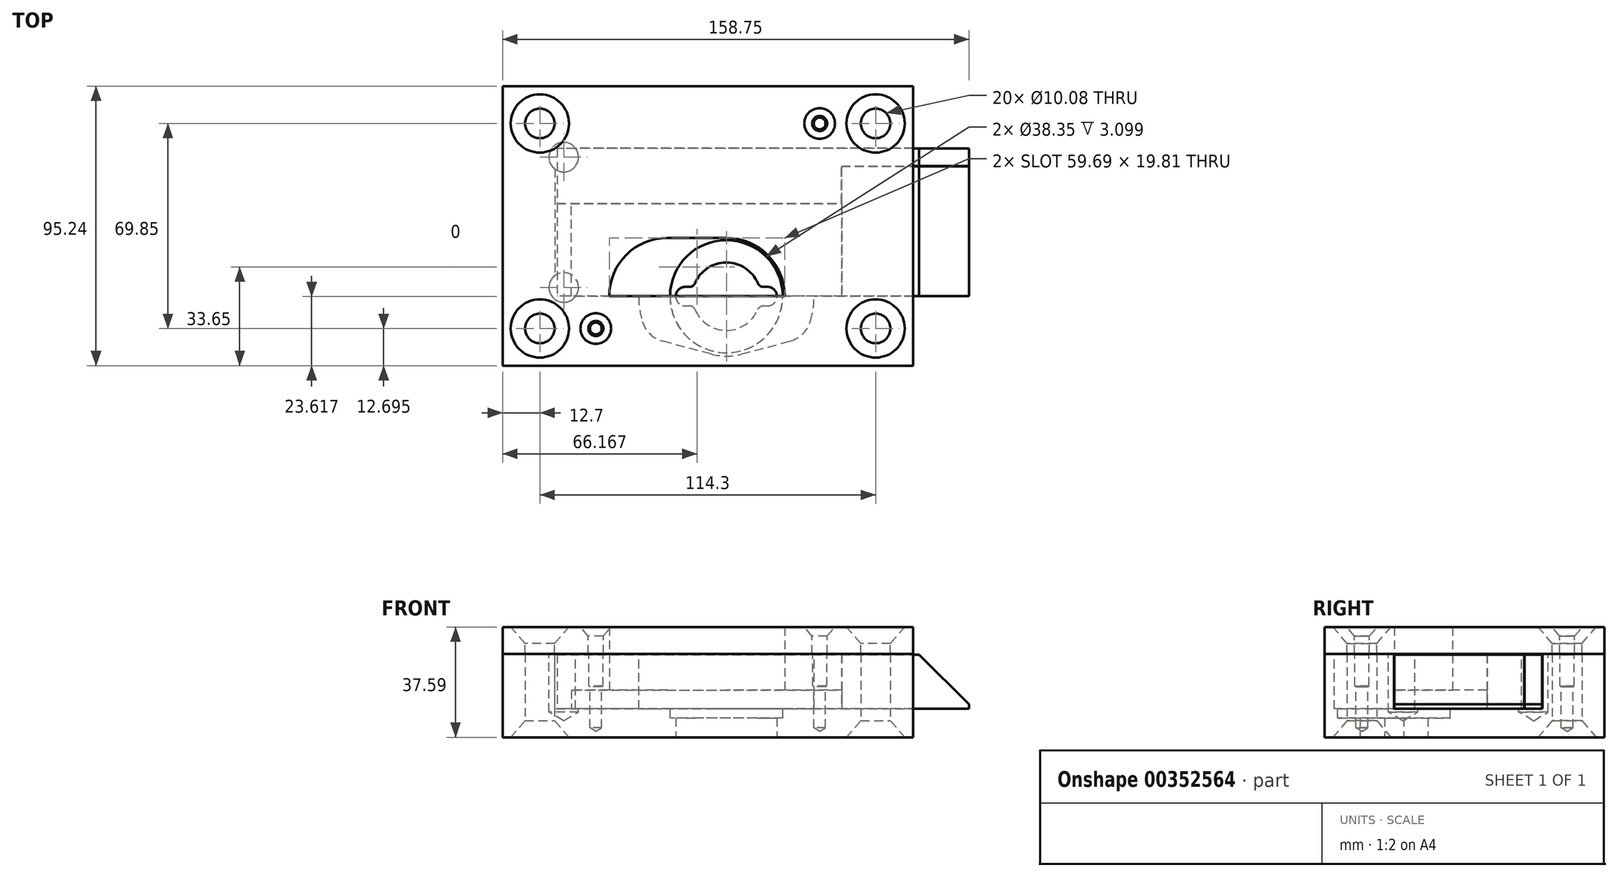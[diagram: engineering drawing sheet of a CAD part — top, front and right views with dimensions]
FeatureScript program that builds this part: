
annotation { "Feature Type Name" : "Feature", "Feature Type Description" : "" }
export const myFeature = defineFeature(function(context is Context, id is Id, definition is map)
    precondition{}
    {
        {
            var Q0;
            Q0=qCreatedBy(makeId("Top.planeOp"),FACE);
            cPlane(context, id + "F0", {"entities" : qUnion([Q0]), "cplaneType" : CPlaneType.OFFSET, "offset" : 6.6 * mm, "oppositeDirection" : true, "width" : 152.4 * mm, "height" : 152.4 * mm});
        }
        {
            var Q0;
            Q0=qCreatedBy(id+"F0.planeOp",FACE);
            var sketch = newSketch(context, id + "F1", { "sketchPlane" : qUnion([Q0])});
            skLineSegment(sketch, "E0.bottom", {"start": v(-69.85, 47.63) * mm, "end": v(69.85, 47.62) * mm});
            skLineSegment(sketch, "E0.top", {"start": v(-69.85, -47.62) * mm, "end": v(69.85, -47.63) * mm});
            skLineSegment(sketch, "E0.left", {"start": v(-69.85, 47.62) * mm, "end": v(-69.85, -47.63) * mm});
            skLineSegment(sketch, "E0.right", {"start": v(69.85, 47.63) * mm, "end": v(69.85, -47.62) * mm});
            skLineSegment(sketch, "E1", {"start": v(0, 47.63) * mm, "end": v(0, -47.63) * mm, "construction": true});
            skLineSegment(sketch, "E2", {"start": v(-69.85, 0) * mm, "end": v(69.85, 0) * mm, "construction": true});
            skPoint(sketch, "E3", {"position": v(-57.15, 34.93) * mm});
            skPoint(sketch, "E4", {"position": v(57.15, 34.93) * mm});
            skPoint(sketch, "E5", {"position": v(57.15, -34.93) * mm});
            skPoint(sketch, "E6", {"position": v(-57.15, -34.93) * mm});
            skArc(sketch, "E7", {"start": v(-4.32, -28.5) * mm, "mid": v(6.35, -35.59) * mm, "end": v(17.02, -28.5) * mm});
            skArc(sketch, "E8.0.startCap", {"start": v(-7.62, -27.25) * mm, "mid": v(-10.87, -24) * mm, "end": v(-7.62, -20.75) * mm});
            skArc(sketch, "E8.0.endCap", {"start": v(20.32, -20.75) * mm, "mid": v(23.57, -24) * mm, "end": v(20.32, -27.25) * mm});
            skLineSegment(sketch, "E8.0.left", {"start": v(-7.62, -20.75) * mm, "end": v(-6.2, -20.75) * mm});
            skLineSegment(sketch, "E8.0.right", {"start": v(-7.62, -27.25) * mm, "end": v(-6.2, -27.25) * mm});
            skLineSegment(sketch, "E9.trimOffspring", {"start": v(18.9, -20.75) * mm, "end": v(20.32, -20.75) * mm});
            skLineSegment(sketch, "E10.trimOffspring", {"start": v(18.9, -27.25) * mm, "end": v(20.32, -27.25) * mm});
            skArc(sketch, "E11.trimOffspring", {"start": v(17.02, -19.5) * mm, "mid": v(6.35, -12.42) * mm, "end": v(-4.32, -19.5) * mm});
            skPoint(sketch, "E12.visualSharp", {"position": v(-4.77, -27.25) * mm});
            skArc(sketch, "E12.filletArc", {"start": v(-4.32, -28.5) * mm, "mid": v(-5.07, -27.6) * mm, "end": v(-6.2, -27.25) * mm});
            skPoint(sketch, "E13.visualSharp", {"position": v(-4.77, -20.75) * mm});
            skArc(sketch, "E13.filletArc", {"start": v(-6.2, -20.75) * mm, "mid": v(-5.07, -20.41) * mm, "end": v(-4.32, -19.5) * mm});
            skPoint(sketch, "E14.visualSharp", {"position": v(17.47, -20.75) * mm});
            skArc(sketch, "E14.filletArc", {"start": v(17.02, -19.5) * mm, "mid": v(17.77, -20.41) * mm, "end": v(18.9, -20.75) * mm});
            skPoint(sketch, "E15.visualSharp", {"position": v(17.47, -27.25) * mm});
            skArc(sketch, "E15.filletArc", {"start": v(18.9, -27.25) * mm, "mid": v(17.77, -27.6) * mm, "end": v(17.02, -28.5) * mm});
            skLineSegment(sketch, "E16", {"start": v(-7.62, -24) * mm, "end": v(20.32, -24) * mm, "construction": true});
            skLineSegment(sketch, "E17", {"start": v(6.35, -9.05) * mm, "end": v(6.35, -38.96) * mm, "construction": true});
            skSolve(sketch);
        }
        {
            var Q0;
            Q0 = qSketchRegion(id + "F1", true);
            extrude(context, id + "F2", {"entities" : qUnion([Q0]), "depth" : 28.45 * mm});
        }
        {
            var Q0;
            Q0=sQuery(id+"F1.wireOp",VERTEX,"E6");
            var Q1;
            Q1=sQuery(id+"F1.wireOp",VERTEX,"E5");
            var Q2;
            Q2=sQuery(id+"F1.wireOp",VERTEX,"E4");
            var Q3;
            Q3=sQuery(id+"F1.wireOp",VERTEX,"E3");
            var Q4;
            Q4=makeQuery(id+"F2.opExtrude","SWEPT_BODY",BODY,{"disambiguationData":[OSD([sQuery(id+"F1.wireOp",EDGE,"E0.bottom"),sQuery(id+"F1.wireOp",EDGE,"E0.top"),sQuery(id+"F1.wireOp",EDGE,"E0.left"),sQuery(id+"F1.wireOp",EDGE,"E0.right"),sQuery(id+"F1.wireOp",EDGE,"E7"),sQuery(id+"F1.wireOp",EDGE,"E8.0.startCap"),sQuery(id+"F1.wireOp",EDGE,"E8.0.endCap"),sQuery(id+"F1.wireOp",EDGE,"E8.0.left"),sQuery(id+"F1.wireOp",EDGE,"E8.0.right"),sQuery(id+"F1.wireOp",EDGE,"E9.trimOffspring"),sQuery(id+"F1.wireOp",EDGE,"E10.trimOffspring"),sQuery(id+"F1.wireOp",EDGE,"E11.trimOffspring"),sQuery(id+"F1.wireOp",EDGE,"E12.filletArc"),sQuery(id+"F1.wireOp",EDGE,"E13.filletArc"),sQuery(id+"F1.wireOp",EDGE,"E14.filletArc"),sQuery(id+"F1.wireOp",EDGE,"E15.filletArc")])]});
            hole(context, id + "F3", {"style" : HoleStyle.C_SINK, "endStyle" : HoleEndStyle.THROUGH, "oppositeDirection" : true, "standardTappedOrClearance" : lookupTablePath({ "standard" : "ANSI", "fit" : "Normal (ASME)", "size" : "3/8", "type" : "Clearance" }), "standardBlindInLast" : lookupTablePath({ "fit" : "Free", "standard" : "ANSI", "size" : "3/8", "type" : "Clearance" }), "holeDiameter" : 10.08 * mm, "cSinkDiameter" : 19.84 * mm, "cSinkAngle" : 82 * degree, "tappedDepth" : 9.65 * mm, "tapClearance" : 16, "locations" : qUnion([Q0, Q1, Q2, Q3]), "scope" : qUnion([Q4])});
        }
        {
            var Q0;
            Q0=makeQuery(id+"F2.opExtrude","CAP_FACE",FACE,{"disambiguationData":[OSD([sQuery(id+"F1.wireOp",EDGE,"E0.bottom"),sQuery(id+"F1.wireOp",EDGE,"E0.top"),sQuery(id+"F1.wireOp",EDGE,"E0.left"),sQuery(id+"F1.wireOp",EDGE,"E0.right"),sQuery(id+"F1.wireOp",EDGE,"E7"),sQuery(id+"F1.wireOp",EDGE,"E8.0.startCap"),sQuery(id+"F1.wireOp",EDGE,"E8.0.endCap"),sQuery(id+"F1.wireOp",EDGE,"E8.0.left"),sQuery(id+"F1.wireOp",EDGE,"E8.0.right"),sQuery(id+"F1.wireOp",EDGE,"E9.trimOffspring"),sQuery(id+"F1.wireOp",EDGE,"E10.trimOffspring"),sQuery(id+"F1.wireOp",EDGE,"E11.trimOffspring"),sQuery(id+"F1.wireOp",EDGE,"E12.filletArc"),sQuery(id+"F1.wireOp",EDGE,"E13.filletArc"),sQuery(id+"F1.wireOp",EDGE,"E14.filletArc"),sQuery(id+"F1.wireOp",EDGE,"E15.filletArc")])],"isStart":false});
            var sketch = newSketch(context, id + "F4", { "sketchPlane" : qUnion([Q0])});
            skLineSegment(sketch, "E18.bottom", {"start": v(69.85, 26.5) * mm, "end": v(-52.07, 26.5) * mm});
            skLineSegment(sketch, "E18.top", {"start": v(69.85, -24) * mm, "end": v(36.2, -24) * mm});
            skLineSegment(sketch, "E18.left", {"start": v(69.85, 26.5) * mm, "end": v(69.85, -24) * mm});
            skLineSegment(sketch, "E18.right", {"start": v(-52.07, 26.5) * mm, "end": v(-52.07, -24) * mm});
            skPoint(sketch, "E19", {"position": v(6.35, -24) * mm});
            skArc(sketch, "E20", {"start": v(34.97, -32.47) * mm, "mid": v(35.89, -28.28) * mm, "end": v(36.2, -24) * mm});
            skCircle(sketch, "E21", {"center": v(6.35, -24) * mm, "radius": 19.18 * mm});
            skLineSegment(sketch, "E22", {"start": v(11.6, -43.63) * mm, "end": v(28.03, -39.23) * mm});
            skLineSegment(sketch, "E23", {"start": v(1.1, -43.63) * mm, "end": v(-15.33, -39.23) * mm});
            skLineSegment(sketch, "E24", {"start": v(6.35, 12.67) * mm, "end": v(6.35, -59.04) * mm, "construction": true});
            skPoint(sketch, "E24.startSnap0", {"position": v(6.35, -12.42) * mm});
            skPoint(sketch, "E25.visualSharp", {"position": v(32.72, -37.97) * mm});
            skArc(sketch, "E25.filletArc", {"start": v(28.03, -39.23) * mm, "mid": v(32.38, -36.76) * mm, "end": v(34.97, -32.47) * mm});
            skPoint(sketch, "E26.visualSharp", {"position": v(-20.02, -37.97) * mm});
            skArc(sketch, "E26.filletArc", {"start": v(-22.27, -32.47) * mm, "mid": v(-19.68, -36.76) * mm, "end": v(-15.33, -39.23) * mm});
            skArc(sketch, "E27.trimOffspring", {"start": v(-23.5, -24) * mm, "mid": v(-23.19, -28.28) * mm, "end": v(-22.27, -32.47) * mm});
            skLineSegment(sketch, "E28.trimOffspring", {"start": v(-23.5, -24) * mm, "end": v(-52.07, -24) * mm});
            skArc(sketch, "E29.trimOffspring", {"start": v(1.1, -43.63) * mm, "mid": v(6.35, -44.32) * mm, "end": v(11.6, -43.63) * mm});
            skPoint(sketch, "E30", {"position": v(-44.96, 26.5) * mm});
            skPoint(sketch, "E31", {"position": v(-52.07, 19.38) * mm});
            skPoint(sketch, "E32", {"position": v(-52.07, -16.9) * mm});
            skPoint(sketch, "E33", {"position": v(-44.96, -24) * mm});
            skCircle(sketch, "E34", {"center": v(-49.02, -20.95) * mm, "radius": 5.08 * mm, "construction": true});
            skPoint(sketch, "E34.third.point", {"position": v(-45.45, -17.33) * mm});
            skCircle(sketch, "E35", {"center": v(-49.02, 23.44) * mm, "radius": 5.08 * mm, "construction": true});
            skPoint(sketch, "E35.third.point", {"position": v(-45.12, 20.19) * mm});
            skPoint(sketch, "E36", {"position": v(38.1, 34.93) * mm});
            skPoint(sketch, "E37", {"position": v(-38.1, -34.93) * mm});
            skPoint(sketch, "E38", {"position": v(57.15, 34.93) * mm});
            skPoint(sketch, "E39", {"position": v(-57.15, -34.93) * mm});
            skSolve(sketch);
        }
        {
            var Q0;
            Q0=makeQuery(id+"F4.imprint","IMPRINT",FACE,{"disambiguationData":[TD([[makeQuery(id+"F4.imprint","IMPRINT",EDGE,{"derivedFrom":sQuery(id+"F4.wireOp",EDGE,"E21")}),1.0]])]});
            extrude(context, id + "F5", {"entities" : qUnion([Q0]), "operationType" : NewBodyOperationType.REMOVE, "oppositeDirection" : true, "depth" : 21.84 * mm});
        }
        {
            var Q0;
            Q0=makeQuery(id+"F4.imprint","IMPRINT",FACE,{"disambiguationData":[TD([[makeQuery(id+"F4.imprint","IMPRINT",EDGE,{"derivedFrom":sQuery(id+"F4.wireOp",EDGE,"E18.bottom")}),1.0]])]});
            extrude(context, id + "F6", {"entities" : qUnion([Q0]), "operationType" : NewBodyOperationType.REMOVE, "oppositeDirection" : true, "depth" : 18.75 * mm});
        }
        {
            var Q0;
            Q0=sQuery(id+"F4.wireOp",VERTEX,"E35.center");
            var Q1;
            Q1=sQuery(id+"F4.wireOp",VERTEX,"E34.center");
            var Q2;
            Q2=makeQuery(id+"F2.opExtrude","SWEPT_BODY",BODY,{"disambiguationData":[OSD([sQuery(id+"F1.wireOp",EDGE,"E0.bottom"),sQuery(id+"F1.wireOp",EDGE,"E0.top"),sQuery(id+"F1.wireOp",EDGE,"E0.left"),sQuery(id+"F1.wireOp",EDGE,"E0.right"),sQuery(id+"F1.wireOp",EDGE,"E7"),sQuery(id+"F1.wireOp",EDGE,"E8.0.startCap"),sQuery(id+"F1.wireOp",EDGE,"E8.0.endCap"),sQuery(id+"F1.wireOp",EDGE,"E8.0.left"),sQuery(id+"F1.wireOp",EDGE,"E8.0.right"),sQuery(id+"F1.wireOp",EDGE,"E9.trimOffspring"),sQuery(id+"F1.wireOp",EDGE,"E10.trimOffspring"),sQuery(id+"F1.wireOp",EDGE,"E11.trimOffspring"),sQuery(id+"F1.wireOp",EDGE,"E12.filletArc"),sQuery(id+"F1.wireOp",EDGE,"E13.filletArc"),sQuery(id+"F1.wireOp",EDGE,"E14.filletArc"),sQuery(id+"F1.wireOp",EDGE,"E15.filletArc")])]});
            hole(context, id + "F7", {"style" : HoleStyle.SIMPLE, "endStyle" : HoleEndStyle.BLIND, "standardTappedOrClearance" : lookupTablePath({ "standard" : "ANSI", "size" : "X (0.4)", "type" : "Drilled" }), "standardBlindInLast" : lookupTablePath({ "standard" : "ANSI", "size" : "X", "type" : "Drilled" }), "holeDiameter" : 10.08 * mm, "holeDepth" : 19.8 * mm, "tappedDepth" : 9.65 * mm, "tapClearance" : 16, "startFromSketch" : true, "locations" : qUnion([Q0, Q1]), "scope" : qUnion([Q2])});
        }
        {
            var Q0;
            Q0=sQuery(id+"F4.wireOp",VERTEX,"E36");
            var Q1;
            Q1=sQuery(id+"F4.wireOp",VERTEX,"E37");
            var Q2;
            Q2=makeQuery(id+"F2.opExtrude","SWEPT_BODY",BODY,{"disambiguationData":[OSD([sQuery(id+"F1.wireOp",EDGE,"E0.bottom"),sQuery(id+"F1.wireOp",EDGE,"E0.top"),sQuery(id+"F1.wireOp",EDGE,"E0.left"),sQuery(id+"F1.wireOp",EDGE,"E0.right"),sQuery(id+"F1.wireOp",EDGE,"E7"),sQuery(id+"F1.wireOp",EDGE,"E8.0.startCap"),sQuery(id+"F1.wireOp",EDGE,"E8.0.endCap"),sQuery(id+"F1.wireOp",EDGE,"E8.0.left"),sQuery(id+"F1.wireOp",EDGE,"E8.0.right"),sQuery(id+"F1.wireOp",EDGE,"E9.trimOffspring"),sQuery(id+"F1.wireOp",EDGE,"E10.trimOffspring"),sQuery(id+"F1.wireOp",EDGE,"E11.trimOffspring"),sQuery(id+"F1.wireOp",EDGE,"E12.filletArc"),sQuery(id+"F1.wireOp",EDGE,"E13.filletArc"),sQuery(id+"F1.wireOp",EDGE,"E14.filletArc"),sQuery(id+"F1.wireOp",EDGE,"E15.filletArc")])]});
            hole(context, id + "F8", {"style" : HoleStyle.SIMPLE, "endStyle" : HoleEndStyle.BLIND, "standardTappedOrClearance" : lookupTablePath({ "standard" : "ANSI", "engagement" : "75%", "pitch" : "32 tpi", "size" : "#10", "type" : "Tapped" }), "standardBlindInLast" : lookupTablePath({ "standard" : "ANSI", "engagement" : "75%", "pitch" : "32 tpi", "size" : "#10", "type" : "Tapped" }), "holeDiameter" : 4.04 * mm, "showTappedDepth" : true, "holeDepth" : 25.2 * mm, "tappedDepth" : 10.92 * mm, "tapClearance" : 18, "locations" : qUnion([Q0, Q1]), "scope" : qUnion([Q2]), "majorDiameter" : 4.83 * mm});
        }
        {
            var Q0;
            Q0=sQuery(id+"F4.wireOp",VERTEX,"E36");
            var Q1;
            Q1=sQuery(id+"F4.wireOp",VERTEX,"E37");
            var Q2;
            Q2=makeQuery(id+"F2.opExtrude","SWEPT_BODY",BODY,{"disambiguationData":[OSD([sQuery(id+"F1.wireOp",EDGE,"E0.bottom"),sQuery(id+"F1.wireOp",EDGE,"E0.top"),sQuery(id+"F1.wireOp",EDGE,"E0.left"),sQuery(id+"F1.wireOp",EDGE,"E0.right"),sQuery(id+"F1.wireOp",EDGE,"E7"),sQuery(id+"F1.wireOp",EDGE,"E8.0.startCap"),sQuery(id+"F1.wireOp",EDGE,"E8.0.endCap"),sQuery(id+"F1.wireOp",EDGE,"E8.0.left"),sQuery(id+"F1.wireOp",EDGE,"E8.0.right"),sQuery(id+"F1.wireOp",EDGE,"E9.trimOffspring"),sQuery(id+"F1.wireOp",EDGE,"E10.trimOffspring"),sQuery(id+"F1.wireOp",EDGE,"E11.trimOffspring"),sQuery(id+"F1.wireOp",EDGE,"E12.filletArc"),sQuery(id+"F1.wireOp",EDGE,"E13.filletArc"),sQuery(id+"F1.wireOp",EDGE,"E14.filletArc"),sQuery(id+"F1.wireOp",EDGE,"E15.filletArc")])]});
            hole(context, id + "F9", {"style" : HoleStyle.C_SINK, "endStyle" : HoleEndStyle.BLIND, "holeDiameter" : 4.83 * mm, "cSinkDiameter" : 5.33 * mm, "cSinkAngle" : 90 * degree, "holeDepth" : 10.92 * mm, "tappedDepth" : 10.93 * mm, "tapClearance" : 18, "locations" : qUnion([Q0, Q1]), "scope" : qUnion([Q2])});
        }
        {
            var Q0;
            {var subQ8=sQuery(id+"F4.wireOp",EDGE,"E18.bottom");Q0=makeQuery(id+"F4.imprint","IMPRINT",FACE,{"disambiguationData":[TD([[makeQuery(id+"F4.imprint","IMPRINT",EDGE,{"derivedFrom":subQ8}),-1.0]])]});}
            var sketch = newSketch(context, id + "F10", { "sketchPlane" : qUnion([Q0])});
            skLineSegment(sketch, "E40.0", {"start": v(-69.85, 47.63) * mm, "end": v(69.85, 47.62) * mm});
            skLineSegment(sketch, "E41.0", {"start": v(-69.85, 47.63) * mm, "end": v(-69.85, -47.63) * mm});
            skLineSegment(sketch, "E42.0", {"start": v(-69.85, -47.62) * mm, "end": v(69.85, -47.63) * mm});
            skLineSegment(sketch, "E43", {"start": v(69.85, 47.62) * mm, "end": v(69.85, -47.63) * mm});
            skSolve(sketch);
        }
        {
            var Q0;
            Q0 = qSketchRegion(id + "F10", true);
            extrude(context, id + "F11", {"entities" : qUnion([Q0]), "depth" : 9.14 * mm});
        }
        {
            var Q0;
            Q0=makeQuery(id+"F11.opExtrude","CAP_FACE",FACE,{"disambiguationData":[OSD([sQuery(id+"F10.wireOp",EDGE,"E40.0"),sQuery(id+"F10.wireOp",EDGE,"E41.0"),sQuery(id+"F10.wireOp",EDGE,"E42.0"),sQuery(id+"F10.wireOp",EDGE,"E43")])],"isStart":false});
            var sketch = newSketch(context, id + "F12", { "sketchPlane" : qUnion([Q0])});
            skPoint(sketch, "E44", {"position": v(-57.15, 34.93) * mm});
            skPoint(sketch, "E45", {"position": v(57.15, 34.93) * mm});
            skPoint(sketch, "E46", {"position": v(57.15, -34.93) * mm});
            skPoint(sketch, "E47", {"position": v(-57.15, -34.93) * mm});
            skPoint(sketch, "E48", {"position": v(38.1, 34.93) * mm});
            skPoint(sketch, "E49", {"position": v(-38.1, -34.93) * mm});
            skSolve(sketch);
        }
        {
            var Q0;
            Q0=sQuery(id+"F12.wireOp",VERTEX,"E44");
            var Q1;
            Q1=sQuery(id+"F12.wireOp",VERTEX,"E45");
            var Q2;
            Q2=sQuery(id+"F12.wireOp",VERTEX,"E46");
            var Q3;
            Q3=sQuery(id+"F12.wireOp",VERTEX,"E47");
            var Q4;
            Q4=makeQuery(id+"F11.opExtrude","SWEPT_BODY",BODY,{"disambiguationData":[OSD([sQuery(id+"F10.wireOp",EDGE,"E40.0"),sQuery(id+"F10.wireOp",EDGE,"E41.0"),sQuery(id+"F10.wireOp",EDGE,"E42.0"),sQuery(id+"F10.wireOp",EDGE,"E43")])]});
            hole(context, id + "F13", {"style" : HoleStyle.C_SINK, "endStyle" : HoleEndStyle.THROUGH, "standardTappedOrClearance" : lookupTablePath({ "standard" : "ANSI", "fit" : "Normal (ASME)", "size" : "3/8", "type" : "Clearance" }), "standardBlindInLast" : lookupTablePath({ "fit" : "Free", "standard" : "ANSI", "size" : "3/8", "type" : "Clearance" }), "holeDiameter" : 10.08 * mm, "cSinkDiameter" : 19.84 * mm, "cSinkAngle" : 82 * degree, "tappedDepth" : 9.65 * mm, "tapClearance" : 16, "locations" : qUnion([Q0, Q1, Q2, Q3]), "scope" : qUnion([Q4])});
        }
        {
            var Q0;
            Q0=sQuery(id+"F12.wireOp",VERTEX,"E48");
            var Q1;
            Q1=sQuery(id+"F12.wireOp",VERTEX,"E49");
            var Q2;
            Q2=makeQuery(id+"F11.opExtrude","SWEPT_BODY",BODY,{"disambiguationData":[OSD([sQuery(id+"F10.wireOp",EDGE,"E40.0"),sQuery(id+"F10.wireOp",EDGE,"E41.0"),sQuery(id+"F10.wireOp",EDGE,"E42.0"),sQuery(id+"F10.wireOp",EDGE,"E43")])]});
            hole(context, id + "F14", {"style" : HoleStyle.C_SINK, "endStyle" : HoleEndStyle.THROUGH, "standardTappedOrClearance" : lookupTablePath({ "standard" : "ANSI", "fit" : "Normal (ASME)", "size" : "#10", "type" : "Clearance" }), "standardBlindInLast" : lookupTablePath({ "fit" : "Free", "standard" : "ANSI", "size" : "#10", "type" : "Clearance" }), "holeDiameter" : 5.1 * mm, "cSinkDiameter" : 10.44 * mm, "cSinkAngle" : 82 * degree, "tappedDepth" : 10.93 * mm, "tapClearance" : 18, "locations" : qUnion([Q0, Q1]), "scope" : qUnion([Q2])});
        }
        {
            var Q0;
            Q0=makeQuery(id+"F6.boolean.opBoolean","COPY",FACE,{"derivedFrom":makeQuery(id+"F6.opExtrude","CAP_FACE",FACE,{"disambiguationData":[OSD([sQuery(id+"F4.wireOp",EDGE,"E18.bottom"),sQuery(id+"F4.wireOp",EDGE,"E18.top"),sQuery(id+"F4.wireOp",EDGE,"E18.left"),sQuery(id+"F4.wireOp",EDGE,"E18.right"),sQuery(id+"F4.wireOp",EDGE,"E20"),sQuery(id+"F4.wireOp",EDGE,"E21"),sQuery(id+"F4.wireOp",EDGE,"E22"),sQuery(id+"F4.wireOp",EDGE,"E23"),sQuery(id+"F4.wireOp",EDGE,"E25.filletArc"),sQuery(id+"F4.wireOp",EDGE,"E26.filletArc"),sQuery(id+"F4.wireOp",EDGE,"E27.trimOffspring"),sQuery(id+"F4.wireOp",EDGE,"E28.trimOffspring"),sQuery(id+"F4.wireOp",EDGE,"E29.trimOffspring")])],"isStart":false})});
            var sketch = newSketch(context, id + "F15", { "sketchPlane" : qUnion([Q0])});
            skLineSegment(sketch, "E50", {"start": v(-51.3, 7.7) * mm, "end": v(45.47, 7.7) * mm});
            skLineSegment(sketch, "E51", {"start": v(45.47, 7.7) * mm, "end": v(45.47, 20.4) * mm});
            skLineSegment(sketch, "E52", {"start": v(45.47, 20.4) * mm, "end": v(88.9, 20.4) * mm});
            skLineSegment(sketch, "E53", {"start": v(88.9, 20.4) * mm, "end": v(88.9, 26.37) * mm});
            skLineSegment(sketch, "E54.0", {"start": v(88.9, 26.37) * mm, "end": v(-51.3, 26.37) * mm});
            skLineSegment(sketch, "E55.0", {"start": v(-51.3, 26.37) * mm, "end": v(-51.3, 7.7) * mm});
            skSolve(sketch);
        }
        {
            var Q0;
            Q0 = qSketchRegion(id + "F15", true);
            extrude(context, id + "F16", {"entities" : qUnion([Q0]), "depth" : 18.5 * mm});
        }
        {
            var Q0;
            Q0=makeQuery(id+"F6.boolean.opBoolean","COPY",FACE,{"derivedFrom":makeQuery(id+"F6.opExtrude","CAP_FACE",FACE,{"disambiguationData":[OSD([sQuery(id+"F4.wireOp",EDGE,"E18.bottom"),sQuery(id+"F4.wireOp",EDGE,"E18.top"),sQuery(id+"F4.wireOp",EDGE,"E18.left"),sQuery(id+"F4.wireOp",EDGE,"E18.right"),sQuery(id+"F4.wireOp",EDGE,"E20"),sQuery(id+"F4.wireOp",EDGE,"E21"),sQuery(id+"F4.wireOp",EDGE,"E22"),sQuery(id+"F4.wireOp",EDGE,"E23"),sQuery(id+"F4.wireOp",EDGE,"E25.filletArc"),sQuery(id+"F4.wireOp",EDGE,"E26.filletArc"),sQuery(id+"F4.wireOp",EDGE,"E27.trimOffspring"),sQuery(id+"F4.wireOp",EDGE,"E28.trimOffspring"),sQuery(id+"F4.wireOp",EDGE,"E29.trimOffspring")])],"isStart":false})});
            var sketch = newSketch(context, id + "F17", { "sketchPlane" : qUnion([Q0])});
            skLineSegment(sketch, "E56.0", {"start": v(-51.3, 7.57) * mm, "end": v(45.6, 7.57) * mm});
            skLineSegment(sketch, "E57.0", {"start": v(-51.3, 7.57) * mm, "end": v(-51.3, -23.88) * mm});
            skLineSegment(sketch, "E58.0", {"start": v(88.9, -23.88) * mm, "end": v(-51.3, -23.88) * mm});
            skLineSegment(sketch, "E59.0", {"start": v(45.6, 20.27) * mm, "end": v(88.9, 20.27) * mm});
            skLineSegment(sketch, "E60.0", {"start": v(45.6, 7.57) * mm, "end": v(45.6, 20.27) * mm});
            skLineSegment(sketch, "E61", {"start": v(88.9, 20.27) * mm, "end": v(88.9, -23.88) * mm});
            skLineSegment(sketch, "E62", {"start": v(-46.48, -23.88) * mm, "end": v(-46.48, 7.57) * mm});
            skLineSegment(sketch, "E63", {"start": v(45.6, 7.57) * mm, "end": v(45.6, -23.88) * mm});
            skArc(sketch, "E64", {"start": v(-13.72, -4.06) * mm, "mid": v(-27.73, -9.87) * mm, "end": v(-33.53, -23.88) * mm});
            skArc(sketch, "E65", {"start": v(26.16, -23.88) * mm, "mid": v(20.36, -9.87) * mm, "end": v(6.35, -4.06) * mm});
            skLineSegment(sketch, "E66", {"start": v(-13.72, -4.06) * mm, "end": v(6.35, -4.06) * mm});
            skSolve(sketch);
        }
        {
            var Q0;
            Q0 = qSketchRegion(id + "F17", true);
            var Q1;
            Q1=makeQuery(id+"F16.opExtrude","CAP_FACE",FACE,{"disambiguationData":[OSD([sQuery(id+"F15.wireOp",EDGE,"E50"),sQuery(id+"F15.wireOp",EDGE,"E51"),sQuery(id+"F15.wireOp",EDGE,"E52"),sQuery(id+"F15.wireOp",EDGE,"E53"),sQuery(id+"F15.wireOp",EDGE,"E54.0"),sQuery(id+"F15.wireOp",EDGE,"E55.0")])],"isStart":false});
            extrude(context, id + "F18", {"entities" : qUnion([Q0]), "endBound" : BoundingType.UP_TO_SURFACE, "endBoundEntityFace" : qUnion([Q1]), "depth" : 25.4 * mm});
        }
        {
            var Q0;
            Q0=makeQuery(id+"F18.opExtrude","SWEPT_FACE",FACE,{"disambiguationData":[OSD([sQuery(id+"F17.wireOp",EDGE,"E58.0")])]});
            var sketch = newSketch(context, id + "F19", { "sketchPlane" : qUnion([Q0])});
            skLineSegment(sketch, "E67.0", {"start": v(88.9, 21.6) * mm, "end": v(88.9, 4.62) * mm});
            skLineSegment(sketch, "E68.0", {"start": v(88.9, 21.6) * mm, "end": v(71.93, 21.6) * mm});
            skLineSegment(sketch, "E69", {"start": v(71.93, 21.6) * mm, "end": v(88.9, 4.62) * mm});
            skSolve(sketch);
        }
        {
            var Q0;
            Q0 = qSketchRegion(id + "F19", true);
            extrude(context, id + "F20", {"entities" : qUnion([Q0]), "operationType" : NewBodyOperationType.REMOVE, "endBound" : BoundingType.THROUGH_ALL, "oppositeDirection" : true, "depth" : 25.4 * mm});
        }
        {
            var Q0;
            {var subQ1=sQuery(id+"F17.wireOp",EDGE,"E64");Q0=makeQuery(id+"F17.imprint","IMPRINT",FACE,{"disambiguationData":[TD([[makeQuery(id+"F17.imprint","IMPRINT",EDGE,{"derivedFrom":subQ1}),1.0]])]});}
            var Q1;
            {var subQ0=sQuery(id+"F17.wireOp",EDGE,"E58.0");var subQ1=makeQuery(id+"F6.boolean.opBoolean","COPY",EDGE,{"derivedFrom":makeQuery(id+"F6.opExtrude","CAP_EDGE",EDGE,{"disambiguationData":[OSD([sQuery(id+"F4.wireOp",EDGE,"E21")])],"isStart":false})});var subQ2=makeQuery(id+"F17.imprint","INTERSECT",VERTEX,{"disambiguationData":[OD(0.0)],"derivedFrom":[subQ1,subQ0]});Q1=makeQuery(id+"F17.imprint","IMPRINT",FACE,{"disambiguationData":[TD([[makeQuery(id+"F17.imprint","IMPRINT",EDGE,{"disambiguationData":[TD([[subQ2,-1.0]])],"derivedFrom":subQ0}),-1.0]])]});}
            extrude(context, id + "F21", {"entities" : qUnion([Q0, Q1]), "operationType" : NewBodyOperationType.REMOVE, "endBound" : BoundingType.THROUGH_ALL, "depth" : 25.4 * mm});
        }
        {
            var Q0;
            {var subQ9=sQuery(id+"F17.wireOp",EDGE,"E63");Q0=makeQuery(id+"F17.imprint","IMPRINT",FACE,{"disambiguationData":[TD([[makeQuery(id+"F17.imprint","IMPRINT",EDGE,{"derivedFrom":subQ9}),-1.0]])]});}
            var Q1;
            {var subQ0=sQuery(id+"F17.wireOp",EDGE,"E62");var subQ1=sQuery(id+"F17.wireOp",EDGE,"E58.0");var subQ2=makeQuery(id+"F17.imprint","INTERSECT",VERTEX,{"derivedFrom":[subQ1,subQ0]});Q1=makeQuery(id+"F17.imprint","IMPRINT",FACE,{"disambiguationData":[TD([[makeQuery(id+"F17.imprint","IMPRINT",EDGE,{"disambiguationData":[TD([[subQ2,1.0]])],"derivedFrom":subQ1}),-1.0]])]});}
            extrude(context, id + "F22", {"entities" : qUnion([Q0, Q1]), "operationType" : NewBodyOperationType.REMOVE, "depth" : 6.35 * mm});
        }
    });
